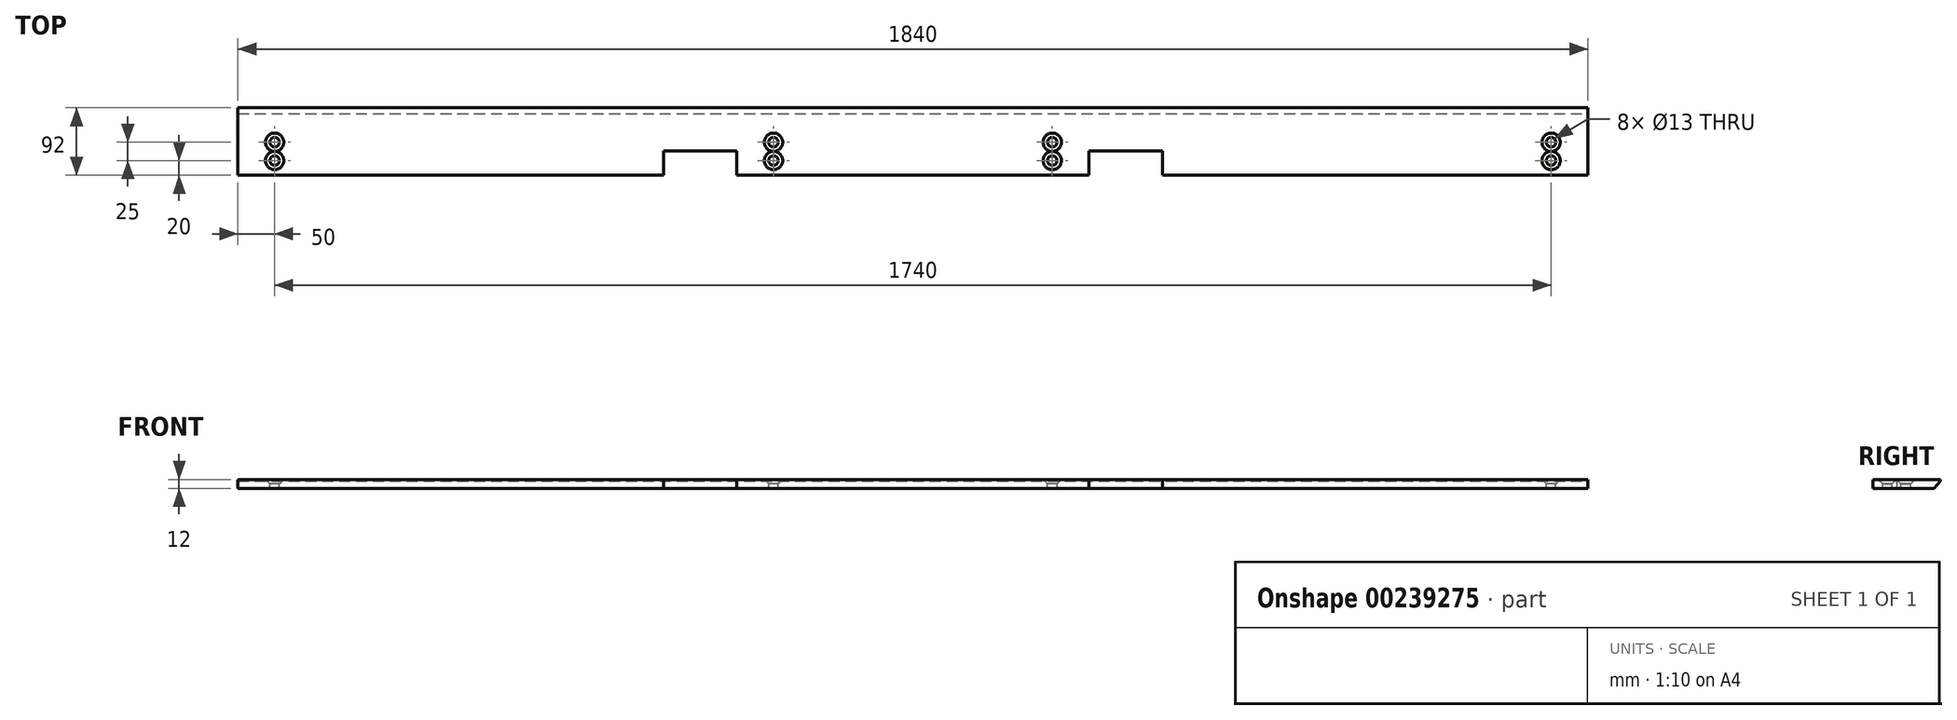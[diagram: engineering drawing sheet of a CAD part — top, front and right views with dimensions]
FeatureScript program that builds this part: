
annotation { "Feature Type Name" : "Feature", "Feature Type Description" : "" }
export const myFeature = defineFeature(function(context is Context, id is Id, definition is map)
    precondition{}
    {
        {
            var Q0;
            Q0=qCreatedBy(makeId("Top.planeOp"),FACE);
            var sketch = newSketch(context, id + "F0", { "sketchPlane" : qUnion([Q0])});
            skLineSegment(sketch, "E0.bottom", {"start": v(-920, 46) * mm, "end": v(920, 46) * mm});
            skLineSegment(sketch, "E0.top", {"start": v(-920, -46) * mm, "end": v(920, -46) * mm});
            skLineSegment(sketch, "E0.left", {"start": v(-920, 46) * mm, "end": v(-920, -46) * mm});
            skLineSegment(sketch, "E0.right", {"start": v(920, 46) * mm, "end": v(920, -46) * mm});
            skPoint(sketch, "E0.middle", {"position": v(0, 0) * mm});
            skSolve(sketch);
        }
        {
            var Q0;
            Q0 = qSketchRegion(id + "F0", true);
            extrude(context, id + "F1", {"entities" : qUnion([Q0]), "endBound" : BoundingType.SYMMETRIC, "depth" : 12 * mm});
        }
        {
            var Q0;
            Q0=makeQuery(id+"F1.opExtrude","CAP_FACE",FACE,{"disambiguationData":[OSD([sQuery(id+"F0.wireOp",EDGE,"E0.bottom"),sQuery(id+"F0.wireOp",EDGE,"E0.top"),sQuery(id+"F0.wireOp",EDGE,"E0.left"),sQuery(id+"F0.wireOp",EDGE,"E0.right")])],"isStart":false});
            var sketch = newSketch(context, id + "F2", { "sketchPlane" : qUnion([Q0])});
            skLineSegment(sketch, "E1", {"start": v(0, 310.06) * mm, "end": v(0, -210.81) * mm, "construction": true});
            skLineSegment(sketch, "E2.0", {"start": v(-920, -46) * mm, "end": v(920, -46) * mm, "construction": true});
            skLineSegment(sketch, "E3.0", {"start": v(-240, 310.06) * mm, "end": v(-240, -210.81) * mm, "construction": true});
            skLineSegment(sketch, "E4.bottom", {"start": v(-240, -46) * mm, "end": v(-340, -46) * mm});
            skLineSegment(sketch, "E4.top", {"start": v(-240, -13) * mm, "end": v(-340, -13) * mm});
            skLineSegment(sketch, "E4.left", {"start": v(-240, -46) * mm, "end": v(-240, -13) * mm});
            skLineSegment(sketch, "E4.right", {"start": v(-340, -46) * mm, "end": v(-340, -13) * mm});
            skLineSegment(sketch, "E5.MirrorCS", {"start": v(340, -46) * mm, "end": v(340, -13) * mm});
            skLineSegment(sketch, "E6.MirrorCS", {"start": v(240, -46) * mm, "end": v(240, -13) * mm});
            skLineSegment(sketch, "E7.MirrorCS", {"start": v(240, -13) * mm, "end": v(340, -13) * mm});
            skLineSegment(sketch, "E8.MirrorCS", {"start": v(240, -46) * mm, "end": v(340, -46) * mm});
            skSolve(sketch);
        }
        {
            var Q0;
            Q0 = qSketchRegion(id + "F2", true);
            extrude(context, id + "F3", {"entities" : qUnion([Q0]), "operationType" : NewBodyOperationType.REMOVE, "endBound" : BoundingType.THROUGH_ALL, "oppositeDirection" : true, "depth" : 25 * mm});
        }
        {
            var Q0;
            Q0=makeQuery(id+"F1.opExtrude","SWEPT_FACE",FACE,{"disambiguationData":[OSD([sQuery(id+"F0.wireOp",EDGE,"E0.right")])]});
            var sketch = newSketch(context, id + "F4", { "sketchPlane" : qUnion([Q0])});
            skLineSegment(sketch, "E9.0", {"start": v(46, 6) * mm, "end": v(-46, 6) * mm, "construction": true});
            skLineSegment(sketch, "E10.0", {"start": v(46, 4) * mm, "end": v(-46, 4) * mm, "construction": true});
            skLineSegment(sketch, "E11.0", {"start": v(46, 6) * mm, "end": v(46, -6) * mm, "construction": true});
            skLineSegment(sketch, "E12", {"start": v(46, 4) * mm, "end": v(37.6, -6) * mm});
            skLineSegment(sketch, "E13", {"start": v(46, 4) * mm, "end": v(46, -6) * mm});
            skLineSegment(sketch, "E14", {"start": v(46, -6) * mm, "end": v(37.6, -6) * mm});
            skSolve(sketch);
        }
        {
            var Q0;
            Q0 = qSketchRegion(id + "F4", true);
            extrude(context, id + "F5", {"entities" : qUnion([Q0]), "operationType" : NewBodyOperationType.REMOVE, "endBound" : BoundingType.THROUGH_ALL, "oppositeDirection" : true, "depth" : 25 * mm});
        }
        {
            var Q0;
            Q0=makeQuery(id+"F1.opExtrude","CAP_FACE",FACE,{"disambiguationData":[OSD([sQuery(id+"F0.wireOp",EDGE,"E0.bottom"),sQuery(id+"F0.wireOp",EDGE,"E0.top"),sQuery(id+"F0.wireOp",EDGE,"E0.left"),sQuery(id+"F0.wireOp",EDGE,"E0.right")])],"isStart":false});
            var sketch = newSketch(context, id + "F6", { "sketchPlane" : qUnion([Q0])});
            skLineSegment(sketch, "E15", {"start": v(0, 160.59) * mm, "end": v(0, -190.3) * mm, "construction": true});
            skLineSegment(sketch, "E16.0", {"start": v(-190, 160.59) * mm, "end": v(-190, -190.3) * mm, "construction": true});
            skLineSegment(sketch, "E17.0", {"start": v(-870, 160.59) * mm, "end": v(-870, -190.3) * mm, "construction": true});
            skLineSegment(sketch, "E18.0", {"start": v(-920, -46) * mm, "end": v(0, -46) * mm, "construction": true});
            skPoint(sketch, "E19.orphan", {"position": v(-340, -46) * mm});
            skLineSegment(sketch, "E20.0", {"start": v(-920, -26) * mm, "end": v(0, -26) * mm, "construction": true});
            skLineSegment(sketch, "E21.0", {"start": v(-920, -1) * mm, "end": v(0, -1) * mm, "construction": true});
            skPoint(sketch, "E22", {"position": v(-870, -1) * mm});
            skPoint(sketch, "E23", {"position": v(-870, -26) * mm});
            skPoint(sketch, "E24", {"position": v(-190, -1) * mm});
            skPoint(sketch, "E25", {"position": v(-190, -26) * mm});
            skPoint(sketch, "E26.MirrorP", {"position": v(870, -1) * mm});
            skPoint(sketch, "E27.MirrorP", {"position": v(870, -26) * mm});
            skPoint(sketch, "E28.MirrorP", {"position": v(190, -1) * mm});
            skPoint(sketch, "E29.MirrorP", {"position": v(190, -26) * mm});
            skSolve(sketch);
        }
        {
            var Q0;
            Q0=sQuery(id+"F6.wireOp",VERTEX,"E22");
            var Q1;
            Q1=sQuery(id+"F6.wireOp",VERTEX,"E23");
            var Q2;
            Q2=sQuery(id+"F6.wireOp",VERTEX,"E24");
            var Q3;
            Q3=sQuery(id+"F6.wireOp",VERTEX,"E25");
            var Q4;
            Q4=sQuery(id+"F6.wireOp",VERTEX,"E29.MirrorP");
            var Q5;
            Q5=sQuery(id+"F6.wireOp",VERTEX,"E28.MirrorP");
            var Q6;
            Q6=sQuery(id+"F6.wireOp",VERTEX,"E26.MirrorP");
            var Q7;
            Q7=sQuery(id+"F6.wireOp",VERTEX,"E27.MirrorP");
            var Q8;
            Q8=makeQuery(id+"F1.opExtrude","SWEPT_BODY",BODY,{"disambiguationData":[OSD([sQuery(id+"F0.wireOp",EDGE,"E0.bottom"),sQuery(id+"F0.wireOp",EDGE,"E0.top"),sQuery(id+"F0.wireOp",EDGE,"E0.left"),sQuery(id+"F0.wireOp",EDGE,"E0.right")])]});
            hole(context, id + "F7", {"style" : HoleStyle.C_SINK, "endStyle" : HoleEndStyle.THROUGH, "holeDiameter" : 13 * mm, "cSinkDiameter" : 25 * mm, "cSinkAngle" : 90 * degree, "locations" : qUnion([Q0, Q1, Q2, Q3, Q4, Q5, Q6, Q7]), "scope" : qUnion([Q8]), "isTappedThrough" : true});
        }
    });
